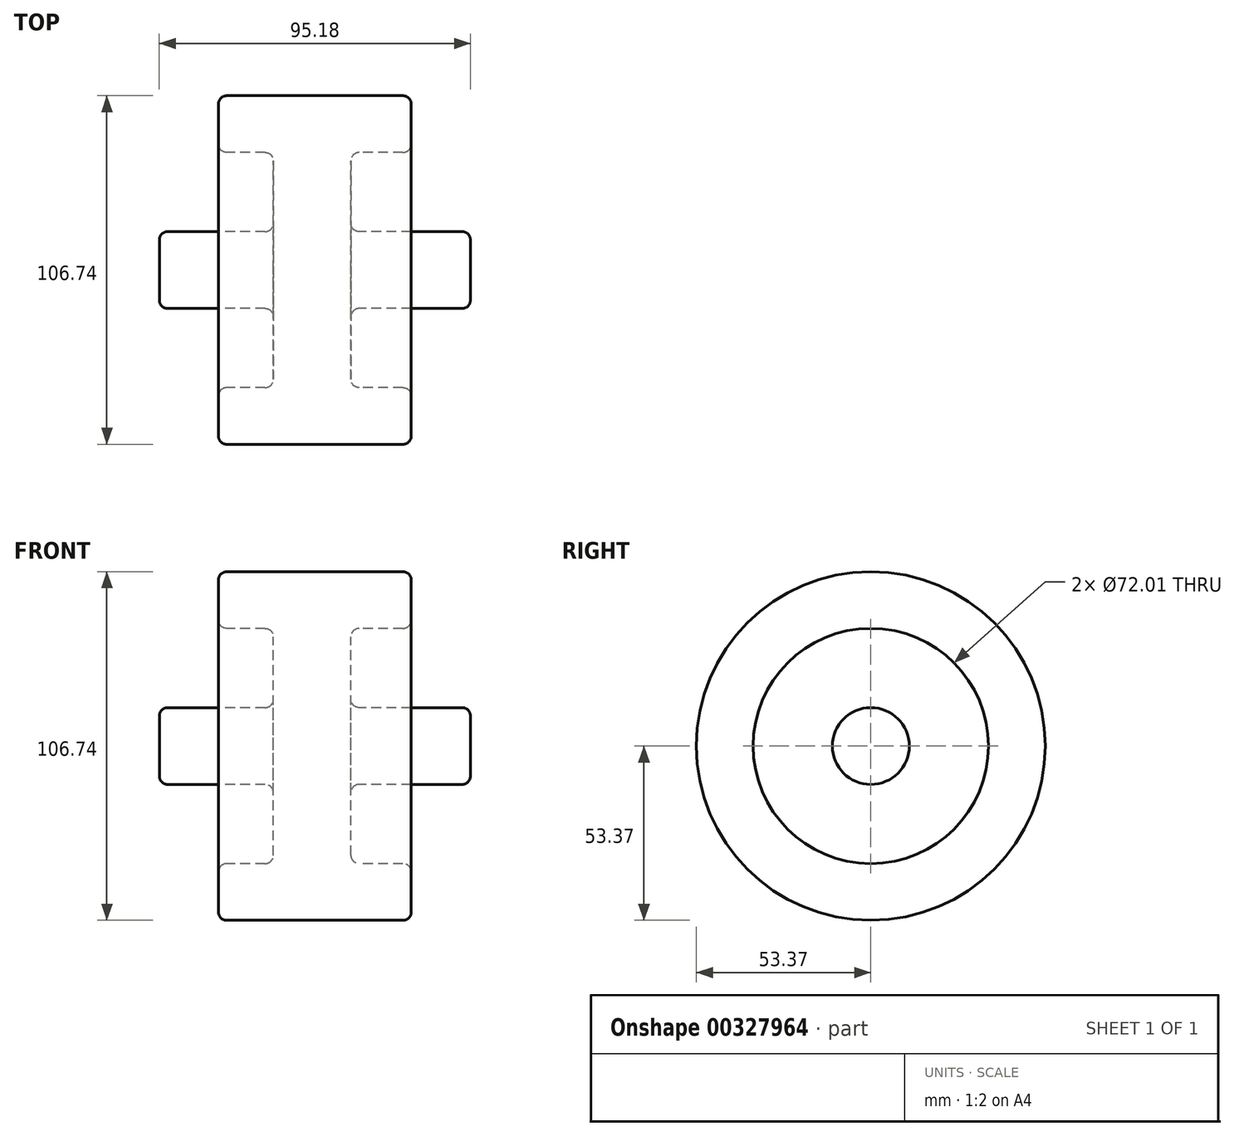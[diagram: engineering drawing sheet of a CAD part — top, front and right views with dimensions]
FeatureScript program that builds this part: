
annotation { "Feature Type Name" : "Feature", "Feature Type Description" : "" }
export const myFeature = defineFeature(function(context is Context, id is Id, definition is map)
    precondition{}
    {
        {
            var Q0;
            Q0=qCreatedBy(makeId("Front.planeOp"),FACE);
            var sketch = newSketch(context, id + "F0", { "sketchPlane" : qUnion([Q0])});
            skLineSegment(sketch, "E0", {"start": v(0, 62.42) * mm, "end": v(0, -38.18) * mm, "construction": true});
            skLineSegment(sketch, "E1", {"start": v(0, 53.37) * mm, "end": v(29.5, 53.37) * mm});
            skLineSegment(sketch, "E2", {"start": v(29.5, 53.37) * mm, "end": v(29.5, 36) * mm});
            skLineSegment(sketch, "E3", {"start": v(29.5, 36) * mm, "end": v(11.04, 36) * mm});
            skLineSegment(sketch, "E4", {"start": v(11.04, 36) * mm, "end": v(11.04, 11.76) * mm});
            skLineSegment(sketch, "E5", {"start": v(11.04, 11.76) * mm, "end": v(47.59, 11.76) * mm});
            skLineSegment(sketch, "E6", {"start": v(47.59, 11.76) * mm, "end": v(47.59, 0) * mm});
            skLineSegment(sketch, "E7", {"start": v(47.59, 0) * mm, "end": v(0, 0) * mm});
            skLineSegment(sketch, "E8.MirrorCS", {"start": v(0, 53.37) * mm, "end": v(-29.5, 53.37) * mm});
            skLineSegment(sketch, "E9.MirrorCS", {"start": v(-29.5, 53.37) * mm, "end": v(-29.5, 36) * mm});
            skLineSegment(sketch, "E10.MirrorCS", {"start": v(-11.04, 36) * mm, "end": v(-11.04, 11.76) * mm});
            skLineSegment(sketch, "E11.MirrorCS", {"start": v(-47.59, 0) * mm, "end": v(0, 0) * mm});
            skLineSegment(sketch, "E12.MirrorCS", {"start": v(-29.5, 36) * mm, "end": v(-11.04, 36) * mm});
            skLineSegment(sketch, "E13.MirrorCS", {"start": v(-47.59, 11.76) * mm, "end": v(-47.59, 0) * mm});
            skLineSegment(sketch, "E14.MirrorCS", {"start": v(-11.04, 11.76) * mm, "end": v(-47.59, 11.76) * mm});
            skSolve(sketch);
        }
        {
            var Q0;
            Q0=makeQuery(id+"F0.imprint","IMPRINT",FACE,{"disambiguationData":[TD([[makeQuery(id+"F0.imprint","IMPRINT",EDGE,{"derivedFrom":sQuery(id+"F0.wireOp",EDGE,"E1")}),-1.0]])]});
            var Q1;
            Q1=sQuery(id+"F0.wireOp",EDGE,"E11.MirrorCS");
            revolve(context, id + "F1", {"entities" : qUnion([Q0]), "axis" : qUnion([Q1]), "revolveType" : RevolveType.FULL});
        }
        {
            var Q0;
            Q0=qCreatedBy(makeId("Right.planeOp"),FACE);
            var sketch = newSketch(context, id + "F2", { "sketchPlane" : qUnion([Q0])});
            skCircle(sketch, "E15", {"center": v(0.18, 0.18) * mm, "radius": 43.93 * mm});
            skSolve(sketch);
        }
        {
            var Q0;
            Q0 = qSketchRegion(id + "F2", true);
            extrude(context, id + "F3", {"entities" : qUnion([Q0]), "operationType" : NewBodyOperationType.ADD, "oppositeDirection" : true, "depth" : 12.7 * mm});
        }
        {
            var Q0;
            Q0=makeQuery(id+"F1.opRevolve","SWEPT_EDGE",EDGE,{"disambiguationData":[OSD([sQuery(id+"F0.wireOp",EDGE,"E8.MirrorCS"),sQuery(id+"F0.wireOp",EDGE,"E9.MirrorCS")])]});
            var Q1;
            Q1=makeQuery(id+"F1.opRevolve","SWEPT_EDGE",EDGE,{"disambiguationData":[OSD([sQuery(id+"F0.wireOp",EDGE,"E9.MirrorCS"),sQuery(id+"F0.wireOp",EDGE,"E12.MirrorCS")])]});
            var Q2;
            Q2=makeQuery(id+"F1.opRevolve","SWEPT_EDGE",EDGE,{"disambiguationData":[OSD([sQuery(id+"F0.wireOp",EDGE,"E13.MirrorCS"),sQuery(id+"F0.wireOp",EDGE,"E14.MirrorCS")])]});
            var Q3;
            Q3=makeQuery(id+"F1.opRevolve","SWEPT_EDGE",EDGE,{"disambiguationData":[OSD([sQuery(id+"F0.wireOp",EDGE,"E1"),sQuery(id+"F0.wireOp",EDGE,"E2")])]});
            var Q4;
            Q4=makeQuery(id+"F1.opRevolve","SWEPT_EDGE",EDGE,{"disambiguationData":[OSD([sQuery(id+"F0.wireOp",EDGE,"E2"),sQuery(id+"F0.wireOp",EDGE,"E3")])]});
            var Q5;
            Q5=makeQuery(id+"F1.opRevolve","SWEPT_EDGE",EDGE,{"disambiguationData":[OSD([sQuery(id+"F0.wireOp",EDGE,"E4"),sQuery(id+"F0.wireOp",EDGE,"E5")])]});
            var Q6;
            Q6=makeQuery(id+"F1.opRevolve","SWEPT_EDGE",EDGE,{"disambiguationData":[OSD([sQuery(id+"F0.wireOp",EDGE,"E3"),sQuery(id+"F0.wireOp",EDGE,"E4")])]});
            var Q7;
            Q7=makeQuery(id+"F3.boolean.opBoolean","INTERSECT",EDGE,{"derivedFrom":[makeQuery(id+"F1.opRevolve","SWEPT_FACE",FACE,{"disambiguationData":[OSD([sQuery(id+"F0.wireOp",EDGE,"E14.MirrorCS")])]}),makeQuery(id+"F3.opExtrude","CAP_FACE",FACE,{"disambiguationData":[OSD([sQuery(id+"F2.wireOp",EDGE,"E15")])],"isStart":false})]});
            var Q8;
            Q8=makeQuery(id+"F3.boolean.opBoolean","INTERSECT",EDGE,{"derivedFrom":[makeQuery(id+"F1.opRevolve","SWEPT_FACE",FACE,{"disambiguationData":[OSD([sQuery(id+"F0.wireOp",EDGE,"E12.MirrorCS")])]}),makeQuery(id+"F3.opExtrude","CAP_FACE",FACE,{"disambiguationData":[OSD([sQuery(id+"F2.wireOp",EDGE,"E15")])],"isStart":false})]});
            var Q9;
            Q9=makeQuery(id+"F1.opRevolve","SWEPT_EDGE",EDGE,{"disambiguationData":[OSD([sQuery(id+"F0.wireOp",EDGE,"E5"),sQuery(id+"F0.wireOp",EDGE,"E6")])]});
            fillet(context, id + "F4", {"entities" : qUnion([Q0, Q1, Q2, Q3, Q4, Q5, Q6, Q7, Q8, Q9]), "radius" : 2.54 * mm, "tangentPropagation" : true, "allowEdgeOverflow" : false});
        }
    });
